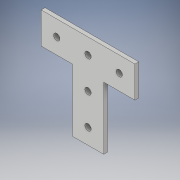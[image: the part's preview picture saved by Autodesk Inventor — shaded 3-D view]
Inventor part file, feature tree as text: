
AUTODESK INVENTOR PART (.ipt)
format: ipt  version: 2018 (Build 220112000, 112)  size: 112,640 bytes
history: native  units: in
note: dims shown in document units (in); Inventor stores cm internally (conversion verified against a paired STEP export)
features: extrude x1, sketch x1
ambient origin geometry x8: Origin, YZ Plane, XZ Plane, XY Plane, X Axis, Y Axis, Z Axis, Center Point
bodies: Solid1 (feature_tree)
feature tree (2):
  extrude  "Extrusion1"  Depth=1.0in
  sketch  "Sketch1"  dims[d0=3.0in d1=1.0in d2=1.0in d3=2.0in d4=1.0in d5=1.0in d6=1.0in d7=0.203in d8=0.125in d9=0.0in]
